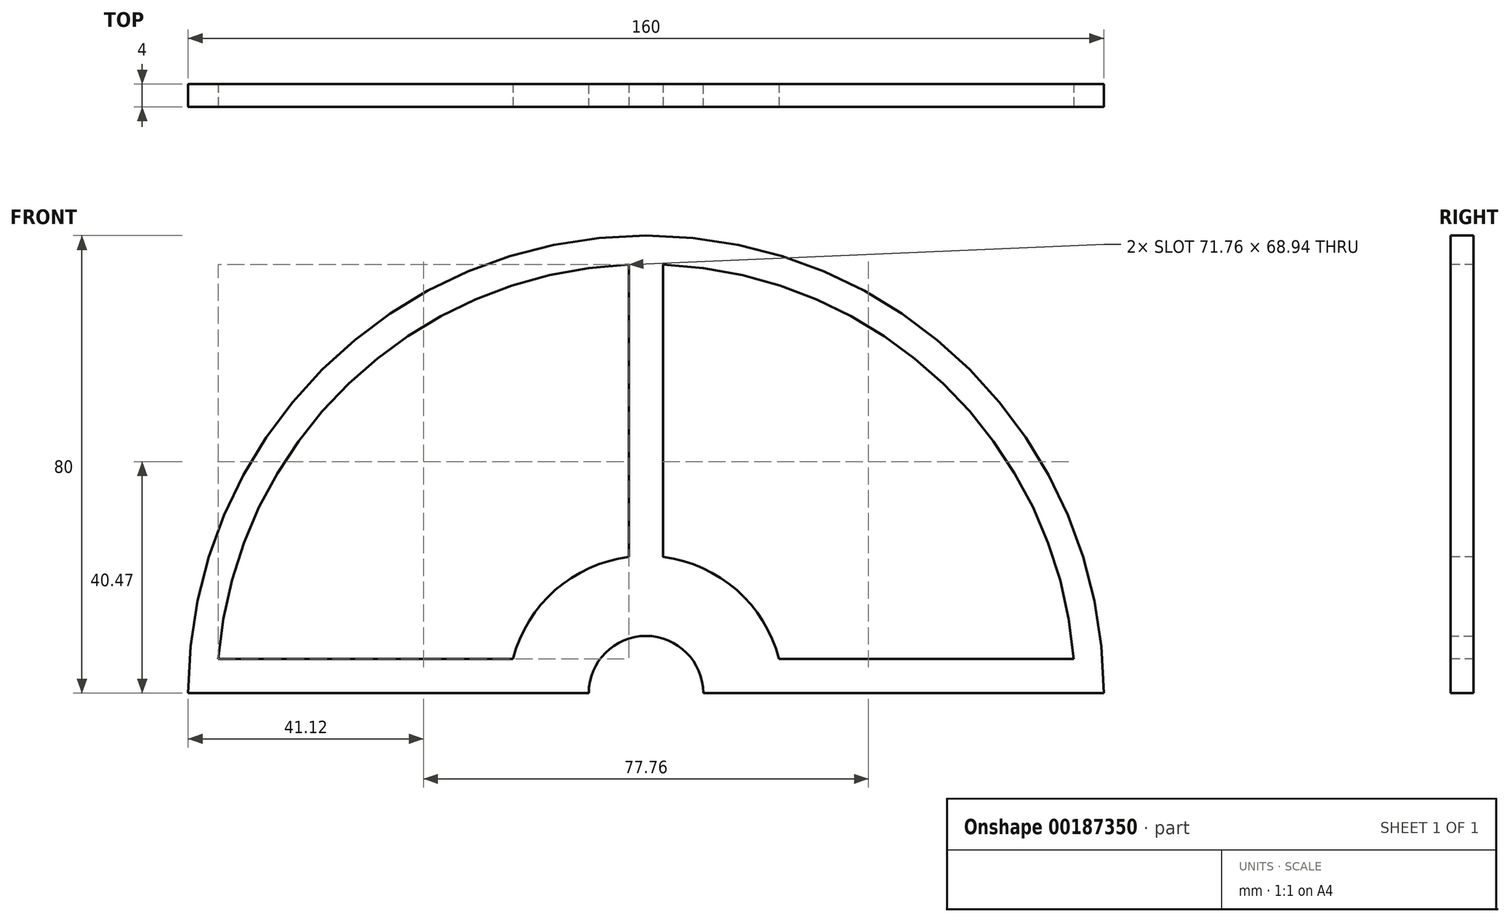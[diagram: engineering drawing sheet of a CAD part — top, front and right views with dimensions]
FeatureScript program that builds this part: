
annotation { "Feature Type Name" : "Feature", "Feature Type Description" : "" }
export const myFeature = defineFeature(function(context is Context, id is Id, definition is map)
    precondition{}
    {
        {
            var Q0;
            Q0=qCreatedBy(makeId("Front.planeOp"),FACE);
            var sketch = newSketch(context, id + "F0", { "sketchPlane" : qUnion([Q0])});
            skCircle(sketch, "E0", {"center": v(0, 0) * mm, "radius": 10 * mm});
            skCircle(sketch, "E1", {"center": v(0, 0) * mm, "radius": 80 * mm});
            skSolve(sketch);
        }
        {
            var Q0;
            Q0 = qSketchRegion(id + "F0", true);
            extrude(context, id + "F1", {"entities" : qUnion([Q0]), "depth" : 4 * mm});
        }
        {
            var Q0;
            Q0=makeQuery(id+"F1.opExtrude","CAP_FACE",FACE,{"disambiguationData":[OSD([sQuery(id+"F0.wireOp",EDGE,"E0"),sQuery(id+"F0.wireOp",EDGE,"E1")])],"isStart":false});
            var sketch = newSketch(context, id + "F2", { "sketchPlane" : qUnion([Q0])});
            skCircle(sketch, "E2", {"center": v(0, 0) * mm, "radius": 14 * mm});
            skCircle(sketch, "E3", {"center": v(0, 0) * mm, "radius": 24 * mm});
            skCircle(sketch, "E4", {"center": v(0, 0) * mm, "radius": 75 * mm});
            skSolve(sketch);
        }
        {
            var Q0;
            Q0=makeQuery(id+"F2.imprint","IMPRINT",FACE,{"disambiguationData":[TD([[makeQuery(id+"F2.imprint","IMPRINT",EDGE,{"derivedFrom":sQuery(id+"F2.wireOp",EDGE,"E3")}),-1.0]])]});
            extrude(context, id + "F3", {"entities" : qUnion([Q0]), "operationType" : NewBodyOperationType.REMOVE, "oppositeDirection" : true, "depth" : 25 * mm});
        }
        {
            var Q0;
            Q0=qCreatedBy(makeId("Front.planeOp"),FACE);
            var sketch = newSketch(context, id + "F4", { "sketchPlane" : qUnion([Q0])});
            skLineSegment(sketch, "E5.bottom", {"start": v(-3, 76.52) * mm, "end": v(3, 76.52) * mm});
            skLineSegment(sketch, "E5.top", {"start": v(-3, 16.52) * mm, "end": v(3, 16.52) * mm});
            skLineSegment(sketch, "E5.left", {"start": v(-3, 76.52) * mm, "end": v(-3, 16.52) * mm});
            skLineSegment(sketch, "E5.right", {"start": v(3, 76.52) * mm, "end": v(3, 16.52) * mm});
            skLineSegment(sketch, "E6.bottom", {"start": v(17.14, 6) * mm, "end": v(77.14, 6) * mm});
            skLineSegment(sketch, "E6.top", {"start": v(17.14, 0) * mm, "end": v(77.14, 0) * mm});
            skLineSegment(sketch, "E6.left", {"start": v(17.14, 6) * mm, "end": v(17.14, 0) * mm});
            skLineSegment(sketch, "E6.right", {"start": v(77.14, 6) * mm, "end": v(77.14, 0) * mm});
            skLineSegment(sketch, "E7", {"start": v(0, 0) * mm, "end": v(76.6, 0) * mm});
            skLineSegment(sketch, "E8", {"start": v(0, 0) * mm, "end": v(0, 75.24) * mm});
            skLineSegment(sketch, "E9", {"start": v(0, 0) * mm, "end": v(0, -79.93) * mm});
            skLineSegment(sketch, "E10.bottom", {"start": v(-3, -20.85) * mm, "end": v(3, -20.85) * mm});
            skLineSegment(sketch, "E10.top", {"start": v(-3, -65.85) * mm, "end": v(3, -65.85) * mm});
            skLineSegment(sketch, "E10.left", {"start": v(-3, -20.85) * mm, "end": v(-3, -65.85) * mm});
            skLineSegment(sketch, "E10.right", {"start": v(3, -20.85) * mm, "end": v(3, -65.85) * mm});
            skLineSegment(sketch, "E11", {"start": v(0, 0) * mm, "end": v(-76.34, 0) * mm});
            skLineSegment(sketch, "E12.bottom", {"start": v(-17.08, 6) * mm, "end": v(-77.08, 6) * mm});
            skLineSegment(sketch, "E12.top", {"start": v(-17.08, 0) * mm, "end": v(-77.08, 0) * mm});
            skLineSegment(sketch, "E12.left", {"start": v(-17.08, 6) * mm, "end": v(-17.08, 0) * mm});
            skLineSegment(sketch, "E12.right", {"start": v(-77.08, 6) * mm, "end": v(-77.08, 0) * mm});
            skSolve(sketch);
        }
        {
            var Q0;
            Q0 = qSketchRegion(id + "F4", true);
            extrude(context, id + "F5", {"entities" : qUnion([Q0]), "operationType" : NewBodyOperationType.ADD, "depth" : 4 * mm});
        }
        {
            var Q0;
            Q0=qCreatedBy(makeId("Front.planeOp"),FACE);
            var sketch = newSketch(context, id + "F6", { "sketchPlane" : qUnion([Q0])});
            skLineSegment(sketch, "E13.bottom", {"start": v(-82.88, 0) * mm, "end": v(87.42, 0) * mm});
            skLineSegment(sketch, "E13.top", {"start": v(-82.88, -83.8) * mm, "end": v(87.42, -83.8) * mm});
            skLineSegment(sketch, "E13.left", {"start": v(-82.88, 0) * mm, "end": v(-82.88, -83.8) * mm});
            skLineSegment(sketch, "E13.right", {"start": v(87.42, 0) * mm, "end": v(87.42, -83.8) * mm});
            skSolve(sketch);
        }
        {
            var Q0;
            Q0 = qSketchRegion(id + "F6", true);
            extrude(context, id + "F7", {"entities" : qUnion([Q0]), "operationType" : NewBodyOperationType.REMOVE, "depth" : 25 * mm});
        }
    });
